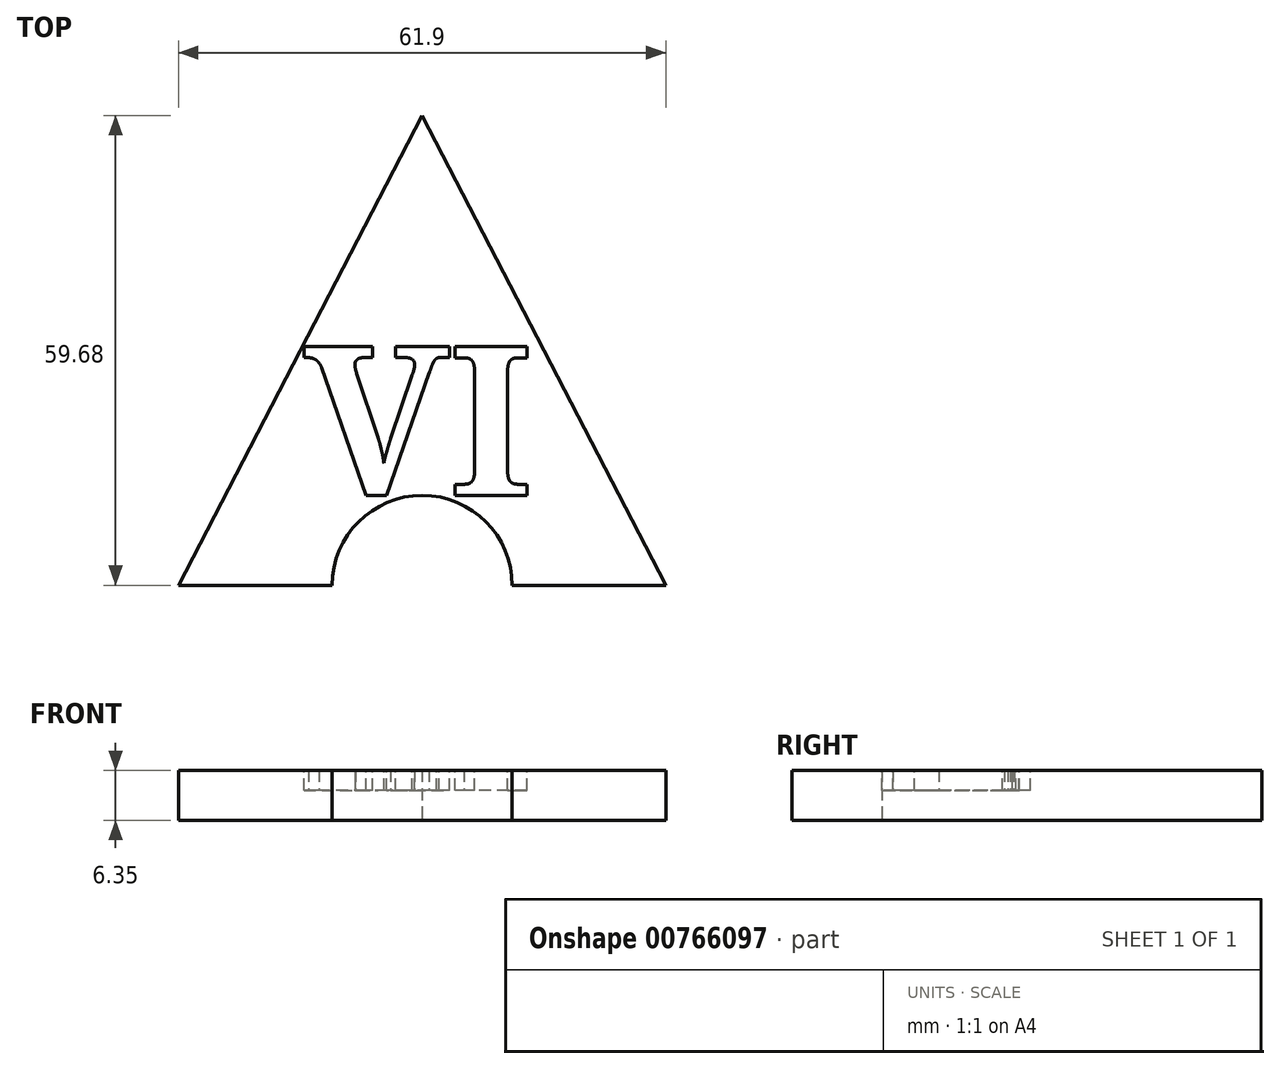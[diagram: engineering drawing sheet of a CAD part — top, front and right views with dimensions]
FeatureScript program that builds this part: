
annotation { "Feature Type Name" : "Feature", "Feature Type Description" : "" }
export const myFeature = defineFeature(function(context is Context, id is Id, definition is map)
    precondition{}
    {
        {
            var Q0;
            Q0=qCreatedBy(makeId("Top.planeOp"),FACE);
            var sketch = newSketch(context, id + "F0", { "sketchPlane" : qUnion([Q0])});
            skCircle(sketch, "E0.cCircle", {"center": v(0, -2.84) * mm, "radius": 17.87 * mm, "construction": true});
            skLineSegment(sketch, "E0.0", {"start": v(30.95, -20.7) * mm, "end": v(-30.95, -20.7) * mm});
            skLineSegment(sketch, "E0.1", {"start": v(-30.95, -20.7) * mm, "end": v(0, 38.98) * mm});
            skLineSegment(sketch, "E0.2", {"start": v(0, 38.98) * mm, "end": v(30.95, -20.7) * mm});
            skPoint(sketch, "E0.0.midPoint", {"position": v(0, -20.7) * mm});
            skSolve(sketch);
        }
        {
            var Q0;
            Q0=makeQuery(id+"F0.imprint","IMPRINT",FACE,{"disambiguationData":[TD([[makeQuery(id+"F0.imprint","IMPRINT",EDGE,{"derivedFrom":sQuery(id+"F0.wireOp",EDGE,"E0.0")}),-1.0]])]});
            extrude(context, id + "F1", {"entities" : qUnion([Q0]), "depth" : 6.35 * mm, "offsetDistance" : 25.4 * mm});
        }
        {
            var Q0;
            Q0=sQuery(id+"F0.wireOp",VERTEX,"E0.0.midPoint");
            var Q1;
            Q1=makeQuery(id+"F1.opExtrude","SWEPT_BODY",BODY,{"disambiguationData":[OSD([sQuery(id+"F0.wireOp",EDGE,"E0.0"),sQuery(id+"F0.wireOp",EDGE,"E0.1"),sQuery(id+"F0.wireOp",EDGE,"E0.2")])]});
            hole(context, id + "F2", {"style" : HoleStyle.SIMPLE, "endStyle" : HoleEndStyle.THROUGH, "oppositeDirection" : true, "holeDiameter" : 22.86 * mm, "majorDiameter" : 6.35 * mm, "isTappedThrough" : true, "tappedDepth" : 12.7 * mm, "tapClearance" : 3, "locations" : qUnion([Q0]), "scope" : qUnion([Q1])});
        }
        {
            var Q0;
            Q0=makeQuery(id+"F1.opExtrude","CAP_FACE",FACE,{"disambiguationData":[OSD([sQuery(id+"F0.wireOp",EDGE,"E0.0"),sQuery(id+"F0.wireOp",EDGE,"E0.1"),sQuery(id+"F0.wireOp",EDGE,"E0.2")])],"isStart":false});
            var sketch = newSketch(context, id + "F3", { "sketchPlane" : qUnion([Q0])});
            skText(sketch, "E1", { "text": "VI", "fontName": "NotoSerif-Bold.ttf"});
            const initialGuessF3  = {"E1": [-0.01503, -0.00927, 1, 0, 0.01905]};
            skSetInitialGuess(sketch, initialGuessF3);
            skSolve(sketch);
        }
        {
            var Q0;
            Q0 = qSketchRegion(id + "F3", true);
            extrude(context, id + "F4", {"entities" : qUnion([Q0]), "operationType" : NewBodyOperationType.REMOVE, "oppositeDirection" : true, "depth" : 2.54 * mm, "offsetDistance" : 25.4 * mm});
        }
    });
